# Revit family: ASL_Door_Sliding_75mm_Jamb_2
name_source: partatom
category: Detail Items
revit_build: Autodesk Revit 2018 (Build: 20170223_1515(x64)
units: mm (PartAtom-declared; Revit-internal decimal feet)

## family parameters
Rotate with component = No
Section Shape = Not Defined
Shared = Yes

## types (3) — shared parameters
Manufacturer = Aluminate Solutions Limited
Technical Info = www.aluminate.nz

## per-type parameters (varying)
| type | ASL Door Suite 75mm | ASL Door Suite 75mm Option | ASL_Woodpile | Flush Infill_PSL_648 | Glazing Unit | Type Comments | Vertical Closer_PSL_355 |
| Close Stile Sliding Door 75mm | Yes | ASL_DoorSuite_Stile_75mm : Closing Stile Sliding Door 75mm | Yes | Yes | No | ASL 350 Sliding System Jamb 2 With 75mm Close Stile | No |
| Glazing | No | ASL_DoorSuite_Stile_75mm : Hinge Stile Hinge Door 75mm | No | No | Yes | ASL 350 Sliding System Jamb 2 With Glazing | Yes |
| Lockset Stile Sliding Door 75mm | Yes | ASL_DoorSuite_Stile_75mm : Lockset Stile Double Action Hinge, Pviot and Sliding Door 75mm | Yes | Yes | No | ASL 350 Sliding System Jamb 2 With 75mm Lockset Stile | No |

## geometry (parser evidence)
native form markers: Sweep x8
no freeform markers — native parametric forms only
